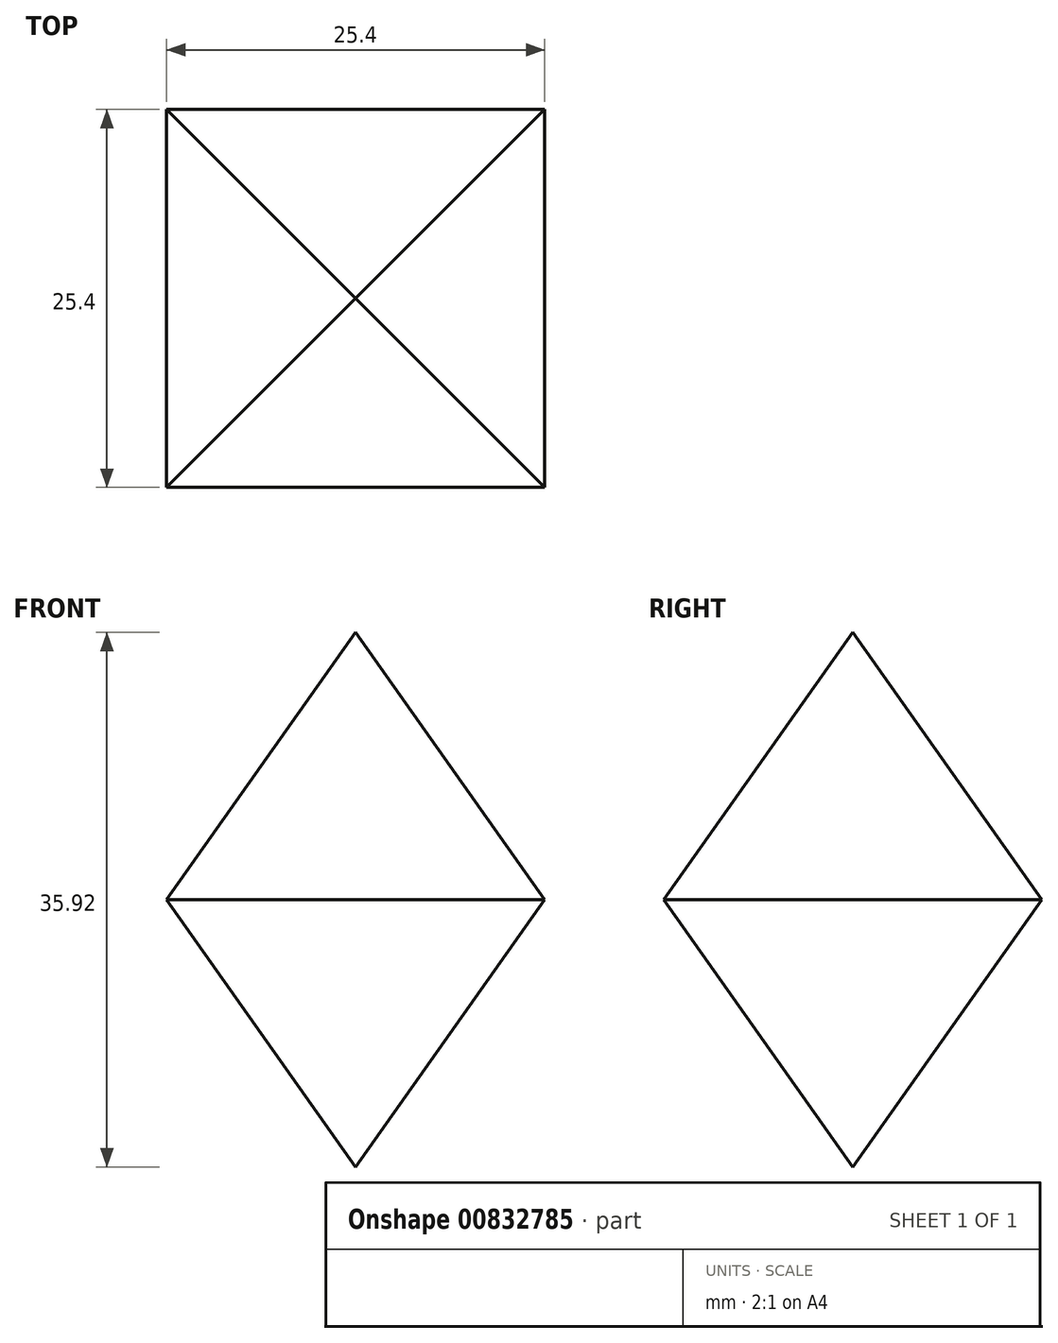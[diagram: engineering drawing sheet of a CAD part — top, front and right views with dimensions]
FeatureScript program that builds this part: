
annotation { "Feature Type Name" : "Feature", "Feature Type Description" : "" }
export const myFeature = defineFeature(function(context is Context, id is Id, definition is map)
    precondition{}
    {
        {
            var Q0;
            Q0=qCreatedBy(makeId("Top.planeOp"),FACE);
            var sketch = newSketch(context, id + "F0", { "sketchPlane" : qUnion([Q0])});
            skLineSegment(sketch, "E0.bottom", {"start": v(12.7, -12.7) * mm, "end": v(-12.7, -12.7) * mm, "construction": true});
            skLineSegment(sketch, "E0.top", {"start": v(12.7, 12.7) * mm, "end": v(-12.7, 12.7) * mm});
            skLineSegment(sketch, "E0.left", {"start": v(12.7, -12.7) * mm, "end": v(12.7, 12.7) * mm, "construction": true});
            skLineSegment(sketch, "E0.right", {"start": v(-12.7, -12.7) * mm, "end": v(-12.7, 12.7) * mm});
            skPoint(sketch, "E0.middle", {"position": v(0, 0) * mm});
            skLineSegment(sketch, "E1", {"start": v(12.7, 12.7) * mm, "end": v(-12.7, -12.7) * mm});
            skSolve(sketch);
        }
        {
            var Q0;
            Q0=qCreatedBy(makeId("Front.planeOp"),FACE);
            var sketch = newSketch(context, id + "F1", { "sketchPlane" : qUnion([Q0])});
            skLineSegment(sketch, "E2", {"start": v(0, 0) * mm, "end": v(-12.7, 0) * mm});
            skLineSegment(sketch, "E3", {"start": v(12.7, 0) * mm, "end": v(0, 0) * mm});
            skLineSegment(sketch, "E4", {"start": v(0, 0) * mm, "end": v(0, 17.96) * mm});
            skSolve(sketch);
        }
        {
            var Q0;
            Q0=sQuery(id+"F0.wireOp",VERTEX,"E0.top.end");
            var Q1;
            Q1=sQuery(id+"F1.wireOp",VERTEX,"E4.end");
            var Q2;
            Q2=sQuery(id+"F0.wireOp",VERTEX,"E0.bottom.end");
            cPlane(context, id + "F2", {"entities" : qUnion([Q0, Q1, Q2]), "cplaneType" : CPlaneType.THREE_POINT, "offset" : 25.4 * mm, "width" : 152.4 * mm, "height" : 152.4 * mm});
        }
        {
            var Q0;
            Q0=sQuery(id+"F0.wireOp",VERTEX,"E0.top.start");
            var Q1;
            Q1=sQuery(id+"F0.wireOp",VERTEX,"E0.top.end");
            var Q2;
            Q2=sQuery(id+"F1.wireOp",VERTEX,"E4.end");
            cPlane(context, id + "F3", {"entities" : qUnion([Q0, Q1, Q2]), "cplaneType" : CPlaneType.THREE_POINT, "offset" : 25.4 * mm, "width" : 152.4 * mm, "height" : 152.4 * mm});
        }
        {
            var Q0;
            Q0 = qSketchRegion(id + "F0", true);
            extrude(context, id + "F4", {"entities" : qUnion([Q0]), "depth" : 25.4 * mm, "offsetDistance" : 25.4 * mm});
        }
        {
            var Q0;
            Q0=qCreatedBy(id+"F2.planeOp",FACE);
            var sketch = newSketch(context, id + "F5", { "sketchPlane" : qUnion([Q0])});
            skLineSegment(sketch, "E5.bottom", {"start": v(-30.26, -23.12) * mm, "end": v(37.63, -23.12) * mm});
            skLineSegment(sketch, "E5.top", {"start": v(-30.26, 39.54) * mm, "end": v(37.63, 39.54) * mm});
            skLineSegment(sketch, "E5.left", {"start": v(-30.26, -23.12) * mm, "end": v(-30.26, 39.54) * mm});
            skLineSegment(sketch, "E5.right", {"start": v(37.63, -23.12) * mm, "end": v(37.63, 39.54) * mm});
            skSolve(sketch);
        }
        {
            var Q0;
            Q0 = qSketchRegion(id + "F5", true);
            extrude(context, id + "F6", {"entities" : qUnion([Q0]), "operationType" : NewBodyOperationType.REMOVE, "depth" : 25.4 * mm, "offsetDistance" : 25.4 * mm});
        }
        {
            var Q0;
            Q0=qCreatedBy(id+"F3.planeOp",FACE);
            var sketch = newSketch(context, id + "F7", { "sketchPlane" : qUnion([Q0])});
            skLineSegment(sketch, "E6.bottom", {"start": v(26.4, -15.73) * mm, "end": v(-36.96, -15.73) * mm});
            skLineSegment(sketch, "E6.top", {"start": v(26.4, 32.46) * mm, "end": v(-36.96, 32.46) * mm});
            skLineSegment(sketch, "E6.left", {"start": v(26.4, -15.73) * mm, "end": v(26.4, 32.46) * mm});
            skLineSegment(sketch, "E6.right", {"start": v(-36.96, -15.73) * mm, "end": v(-36.96, 32.46) * mm});
            skSolve(sketch);
        }
        {
            var Q0;
            Q0 = qSketchRegion(id + "F7", true);
            extrude(context, id + "F8", {"entities" : qUnion([Q0]), "operationType" : NewBodyOperationType.REMOVE, "oppositeDirection" : true, "depth" : 25.4 * mm, "offsetDistance" : 25.4 * mm});
        }
        {
            var Q0;
            Q0=makeQuery(id+"F4.opExtrude","SWEPT_BODY",BODY,{"disambiguationData":[OSD([sQuery(id+"F0.wireOp",EDGE,"E0.top"),sQuery(id+"F0.wireOp",EDGE,"E0.right"),sQuery(id+"F0.wireOp",EDGE,"E1")])]});
            var Q1;
            Q1=makeQuery(id+"F4.opExtrude","SWEPT_FACE",FACE,{"disambiguationData":[OSD([sQuery(id+"F0.wireOp",EDGE,"E1")])]});
            mirror(context, id + "F9", {"operationType" : NewBodyOperationType.ADD, "entities" : qUnion([Q0]), "mirrorPlane" : qUnion([Q1])});
        }
        {
            var Q0;
            Q0=makeQuery(id+"F4.opExtrude","SWEPT_BODY",BODY,{"disambiguationData":[OSD([sQuery(id+"F0.wireOp",EDGE,"E0.top"),sQuery(id+"F0.wireOp",EDGE,"E0.right"),sQuery(id+"F0.wireOp",EDGE,"E1")])]});
            var Q1;
            {var subQ0=makeQuery(id+"F4.opExtrude","CAP_FACE",FACE,{"disambiguationData":[OSD([sQuery(id+"F0.wireOp",EDGE,"E0.top"),sQuery(id+"F0.wireOp",EDGE,"E0.right"),sQuery(id+"F0.wireOp",EDGE,"E1")])],"isStart":true});Q1=makeQuery(id+"F9.boolean.opBoolean","MERGE",FACE,{"derivedFrom":[subQ0,makeQuery(id+"F9.opPattern","COPY",FACE,{"derivedFrom":subQ0,"instanceName":"1"})]});}
            mirror(context, id + "F10", {"operationType" : NewBodyOperationType.ADD, "entities" : qUnion([Q0]), "mirrorPlane" : qUnion([Q1])});
        }
    });
